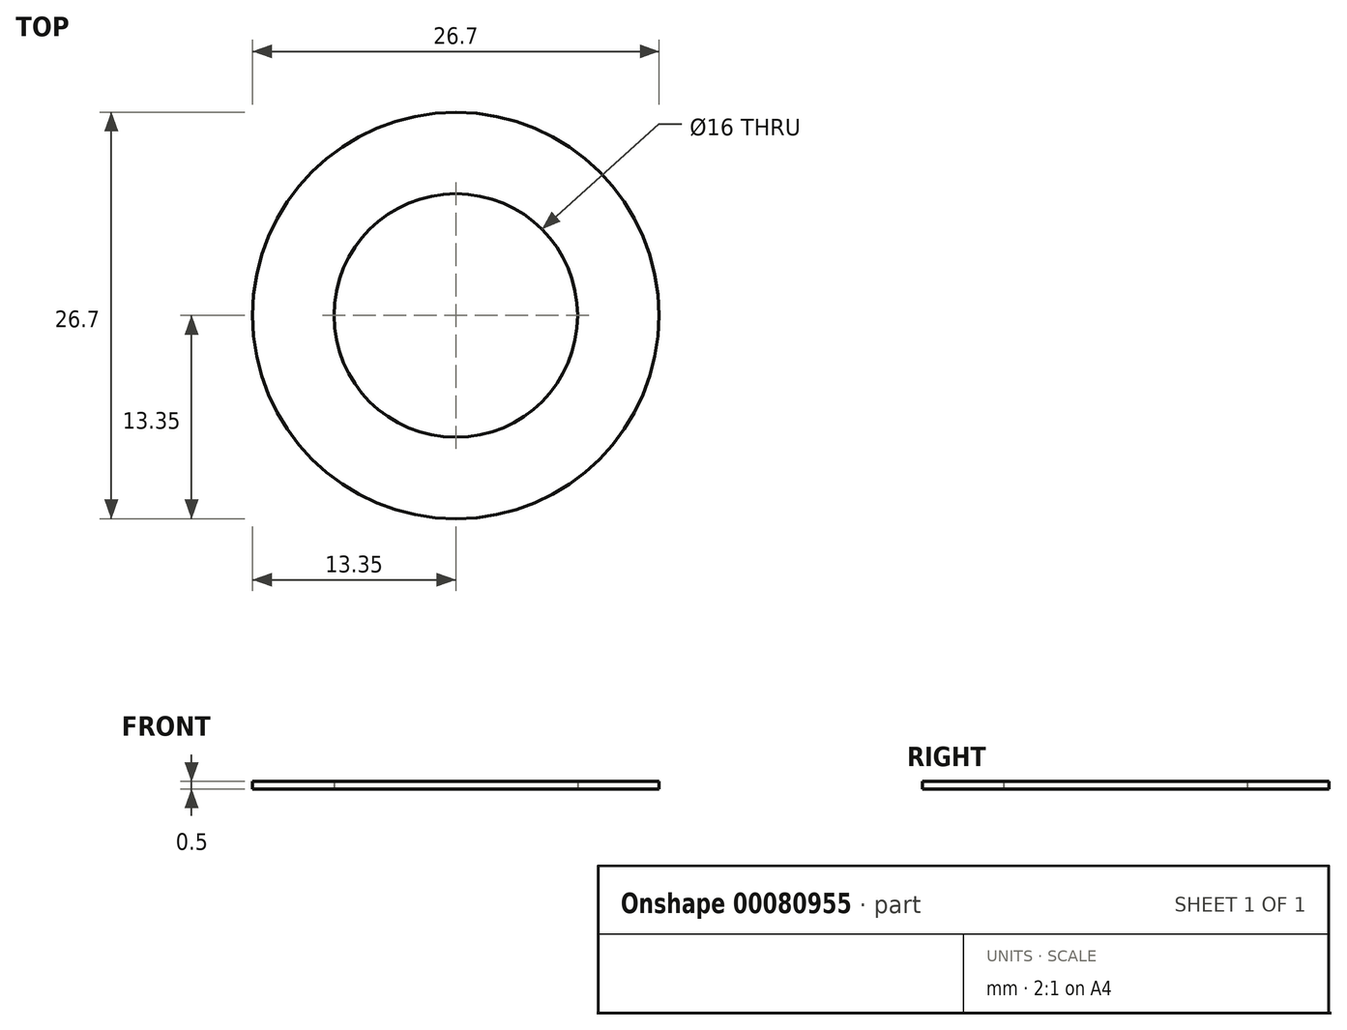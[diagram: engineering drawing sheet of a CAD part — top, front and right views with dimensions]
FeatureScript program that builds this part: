
annotation { "Feature Type Name" : "Feature", "Feature Type Description" : "" }
export const myFeature = defineFeature(function(context is Context, id is Id, definition is map)
    precondition{}
    {
        {
            var Q0;
            Q0=qCreatedBy(makeId("Top.planeOp"),FACE);
            var sketch = newSketch(context, id + "F0", { "sketchPlane" : qUnion([Q0])});
            skCircle(sketch, "E0", {"center": v(0, 0) * mm, "radius": 8 * mm});
            skCircle(sketch, "E1", {"center": v(0, 0) * mm, "radius": 13.35 * mm});
            skCircle(sketch, "E2", {"center": v(0, 0) * mm, "radius": 10.78 * mm});
            skPoint(sketch, "E3", {"position": v(0, 10.78) * mm});
            skPoint(sketch, "E4", {"position": v(0, -10.78) * mm});
            skPoint(sketch, "E5", {"position": v(10.78, 0) * mm});
            skPoint(sketch, "E6", {"position": v(-10.78, 0) * mm});
            skPoint(sketch, "E7", {"position": v(-9.67, 4.78) * mm});
            skPoint(sketch, "E8", {"position": v(-5.84, 9.07) * mm});
            skPoint(sketch, "E9", {"position": v(5.84, 9.07) * mm});
            skPoint(sketch, "E10", {"position": v(9.83, 4.67) * mm});
            skPoint(sketch, "E11", {"position": v(9.5, -5.1) * mm});
            skPoint(sketch, "E12", {"position": v(5.51, -9.27) * mm});
            skPoint(sketch, "E13", {"position": v(-5.51, -9.27) * mm});
            skPoint(sketch, "E14", {"position": v(-9.3, -5.46) * mm});
            skSolve(sketch);
        }
        {
            var Q0;
            Q0=makeQuery(id+"F0.imprint","IMPRINT",FACE,{"disambiguationData":[TD([[makeQuery(id+"F0.imprint","IMPRINT",EDGE,{"derivedFrom":sQuery(id+"F0.wireOp",EDGE,"E0")}),-1.0]])]});
            var Q1;
            Q1=makeQuery(id+"F0.imprint","IMPRINT",FACE,{"disambiguationData":[TD([[makeQuery(id+"F0.imprint","IMPRINT",EDGE,{"derivedFrom":sQuery(id+"F0.wireOp",EDGE,"E1")}),1.0]])]});
            extrude(context, id + "F1", {"entities" : qUnion([Q0, Q1]), "depth" : .5 * mm});
        }
    });
